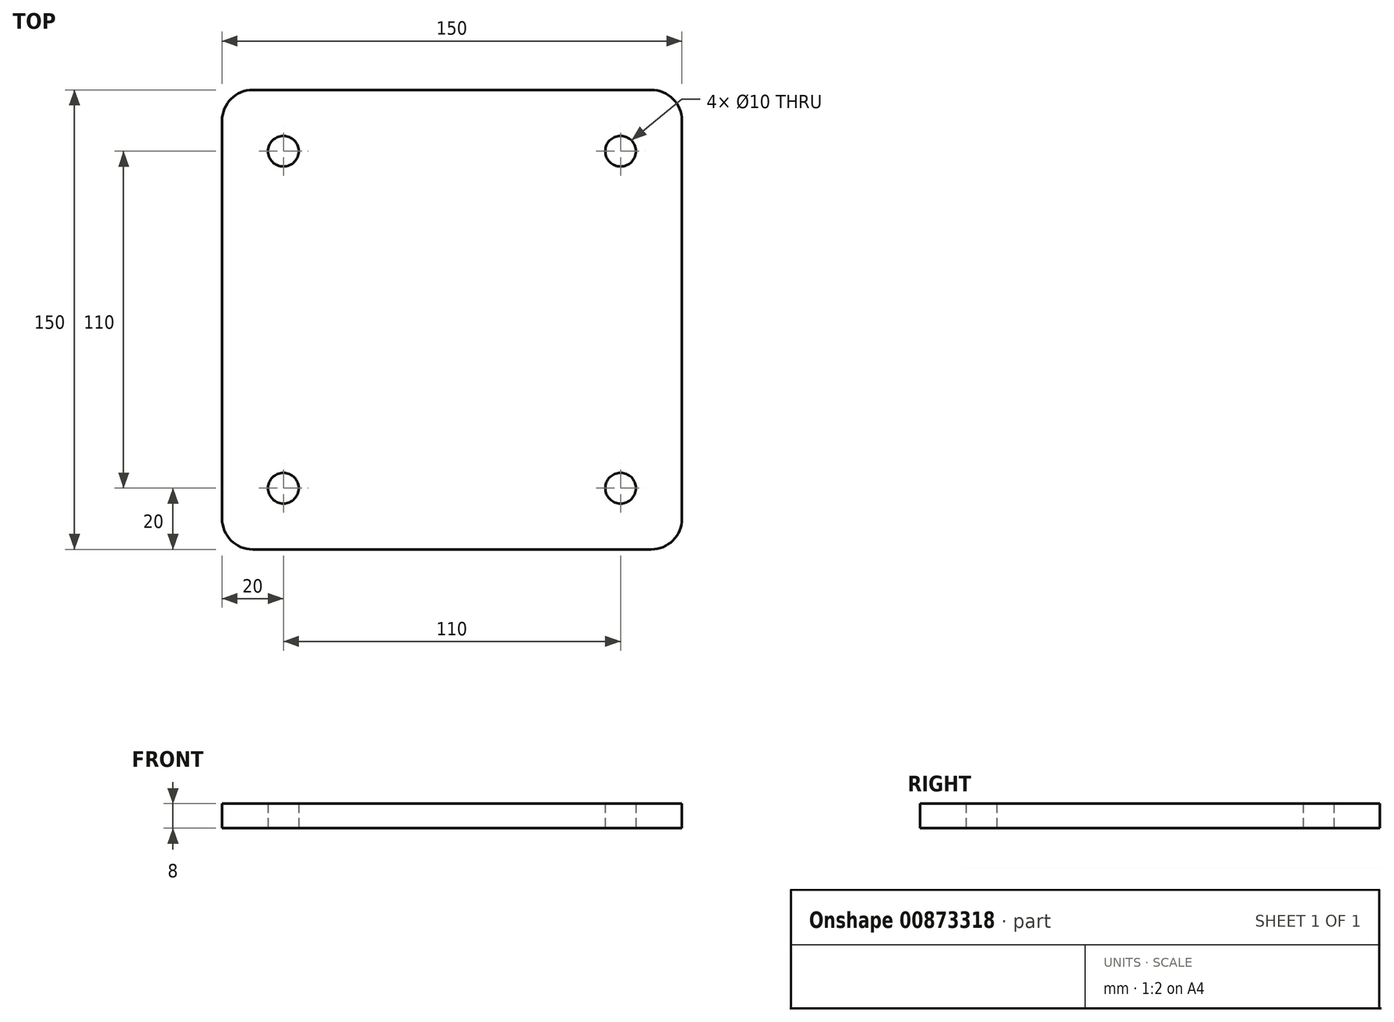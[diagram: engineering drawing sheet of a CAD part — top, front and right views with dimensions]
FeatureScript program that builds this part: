
annotation { "Feature Type Name" : "Feature", "Feature Type Description" : "" }
export const myFeature = defineFeature(function(context is Context, id is Id, definition is map)
    precondition{}
    {
        {
            var Q0;
            Q0=qCreatedBy(makeId("Top.planeOp"),FACE);
            var sketch = newSketch(context, id + "F0", { "sketchPlane" : qUnion([Q0])});
            skLineSegment(sketch, "E0.bottom", {"start": v(65, -75) * mm, "end": v(-65, -75) * mm});
            skLineSegment(sketch, "E0.top", {"start": v(65, 75) * mm, "end": v(-65, 75) * mm});
            skLineSegment(sketch, "E0.left", {"start": v(75, -65) * mm, "end": v(75, 65) * mm});
            skLineSegment(sketch, "E0.right", {"start": v(-75, -65) * mm, "end": v(-75, 65) * mm});
            skPoint(sketch, "E0.middle", {"position": v(0, 0) * mm});
            skCircle(sketch, "E1", {"center": v(-55, 55) * mm, "radius": 5 * mm});
            skCircle(sketch, "E2.MirrorC", {"center": v(55, 55) * mm, "radius": 5 * mm});
            skCircle(sketch, "E3.MirrorC", {"center": v(-55, -55) * mm, "radius": 5 * mm});
            skCircle(sketch, "E4.MirrorC", {"center": v(55, -55) * mm, "radius": 5 * mm});
            skPoint(sketch, "E5.visualSharp", {"position": v(75, 75) * mm});
            skArc(sketch, "E5.filletArc", {"start": v(75, 65) * mm, "mid": v(72.07, 72.07) * mm, "end": v(65, 75) * mm});
            skPoint(sketch, "E6.visualSharp", {"position": v(75, -75) * mm});
            skArc(sketch, "E6.filletArc", {"start": v(65, -75) * mm, "mid": v(72.07, -72.07) * mm, "end": v(75, -65) * mm});
            skPoint(sketch, "E7.visualSharp", {"position": v(-75, -75) * mm});
            skArc(sketch, "E7.filletArc", {"start": v(-75, -65) * mm, "mid": v(-72.07, -72.07) * mm, "end": v(-65, -75) * mm});
            skPoint(sketch, "E8.visualSharp", {"position": v(-75, 75) * mm});
            skArc(sketch, "E8.filletArc", {"start": v(-65, 75) * mm, "mid": v(-72.07, 72.07) * mm, "end": v(-75, 65) * mm});
            skSolve(sketch);
        }
        {
            var Q0;
            Q0=makeQuery(id+"F0.imprint","IMPRINT",FACE,{"disambiguationData":[TD([[makeQuery(id+"F0.imprint","IMPRINT",EDGE,{"derivedFrom":sQuery(id+"F0.wireOp",EDGE,"E0.bottom")}),-1.0]])]});
            extrude(context, id + "F1", {"entities" : qUnion([Q0]), "depth" : 8 * mm, "offsetDistance" : 25 * mm});
        }
    });
